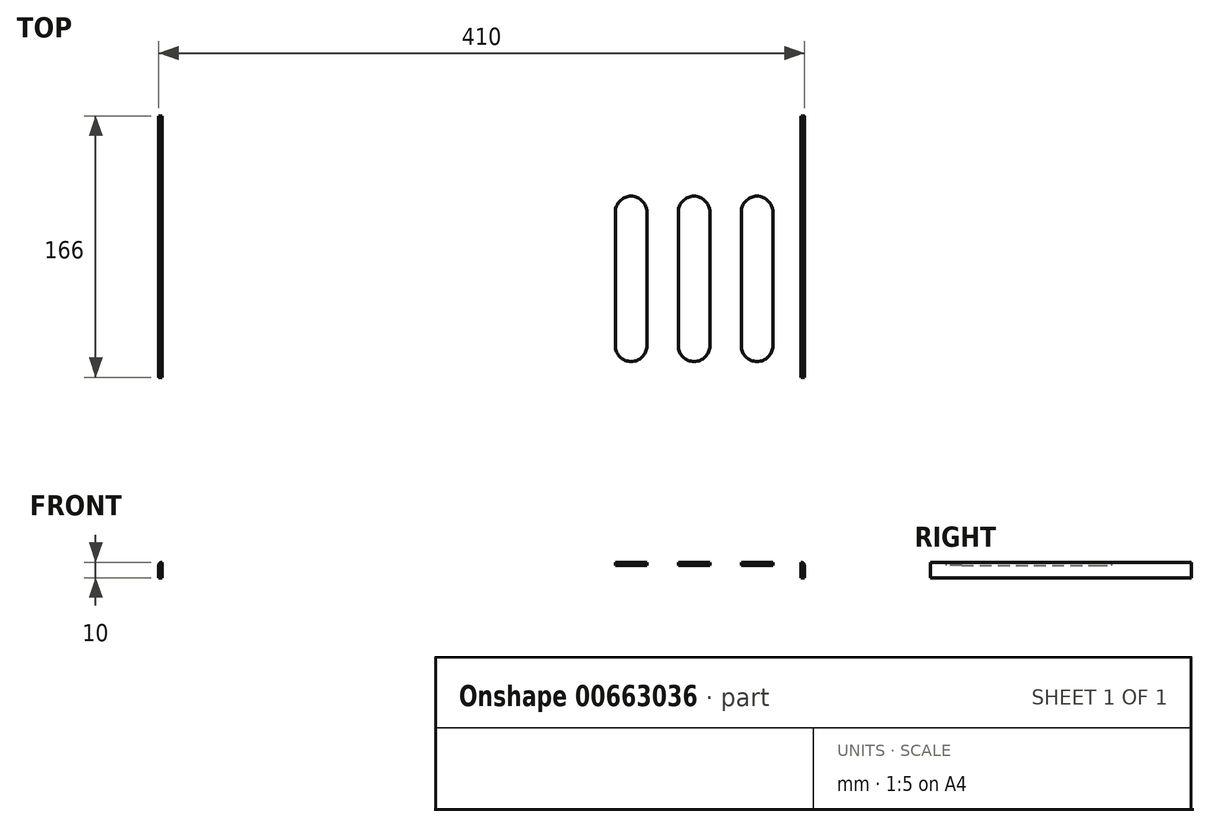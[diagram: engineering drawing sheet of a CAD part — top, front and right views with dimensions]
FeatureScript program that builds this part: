
annotation { "Feature Type Name" : "Feature", "Feature Type Description" : "" }
export const myFeature = defineFeature(function(context is Context, id is Id, definition is map)
    precondition{}
    {
        {
            var Q0;
            Q0=qCreatedBy(makeId("Front.planeOp"),FACE);
            var sketch = newSketch(context, id + "F0", { "sketchPlane" : qUnion([Q0])});
            skLineSegment(sketch, "E0", {"start": v(0, 0) * mm, "end": v(0, 8) * mm});
            skLineSegment(sketch, "E1", {"start": v(2, 10) * mm, "end": v(408, 10) * mm});
            skLineSegment(sketch, "E2", {"start": v(410, 8) * mm, "end": v(410, 0) * mm});
            skLineSegment(sketch, "E3.0", {"start": v(408, 8) * mm, "end": v(408, 0) * mm});
            skLineSegment(sketch, "E3.1", {"start": v(2, 8) * mm, "end": v(408, 8) * mm});
            skLineSegment(sketch, "E3.2", {"start": v(2, 0) * mm, "end": v(2, 8) * mm});
            skLineSegment(sketch, "E4", {"start": v(408, 0) * mm, "end": v(410, 0) * mm});
            skLineSegment(sketch, "E5", {"start": v(0, 0) * mm, "end": v(2, 0) * mm});
            skPoint(sketch, "E6.visualSharp", {"position": v(410, 10) * mm});
            skArc(sketch, "E6.filletArc", {"start": v(410, 8) * mm, "mid": v(409.41, 9.41) * mm, "end": v(408, 10) * mm});
            skPoint(sketch, "E7.visualSharp", {"position": v(0, 10) * mm});
            skArc(sketch, "E7.filletArc", {"start": v(2, 10) * mm, "mid": v(0.59, 9.41) * mm, "end": v(0, 8) * mm});
            skSolve(sketch);
        }
        {
            var Q0;
            Q0=makeQuery(id+"F0.imprint","IMPRINT",FACE,{"disambiguationData":[TD([[makeQuery(id+"F0.imprint","IMPRINT",EDGE,{"derivedFrom":sQuery(id+"F0.wireOp",EDGE,"E0")}),-1.0]])]});
            extrude(context, id + "F1", {"entities" : qUnion([Q0]), "oppositeDirection" : true, "depth" : 166 * mm, "offsetDistance" : 25 * mm});
        }
        {
            var Q0;
            Q0=makeQuery(id+"F1.opExtrude","SWEPT_FACE",FACE,{"disambiguationData":[OSD([sQuery(id+"F0.wireOp",EDGE,"E3.1")])]});
            var sketch = newSketch(context, id + "F2", { "sketchPlane" : qUnion([Q0])});
            skPoint(sketch, "E8", {"position": v(300, -62.5) * mm});
            skPoint(sketch, "E9", {"position": v(340, -62.5) * mm});
            skPoint(sketch, "E10", {"position": v(380, -62.5) * mm});
            skPoint(sketch, "E11", {"position": v(300, -166) * mm});
            skPoint(sketch, "E12", {"position": v(340, -166) * mm});
            skPoint(sketch, "E13", {"position": v(380, -166) * mm});
            skLineSegment(sketch, "E14", {"start": v(300, -20) * mm, "end": v(300, -105) * mm});
            skArc(sketch, "E15.0.startCap", {"start": v(290, -20) * mm, "mid": v(300, -10) * mm, "end": v(310, -20) * mm});
            skArc(sketch, "E15.0.endCap", {"start": v(310, -105) * mm, "mid": v(300, -115) * mm, "end": v(290, -105) * mm});
            skLineSegment(sketch, "E15.0.left", {"start": v(310, -20) * mm, "end": v(310, -105) * mm});
            skLineSegment(sketch, "E15.0.right", {"start": v(290, -20) * mm, "end": v(290, -105) * mm});
            skLineSegment(sketch, "E16", {"start": v(340, -20) * mm, "end": v(340, -105) * mm});
            skLineSegment(sketch, "E17", {"start": v(380, -20) * mm, "end": v(380, -105) * mm});
            skArc(sketch, "E18.0.startCap", {"start": v(330, -20) * mm, "mid": v(340, -10) * mm, "end": v(350, -20) * mm});
            skArc(sketch, "E18.0.endCap", {"start": v(350, -105) * mm, "mid": v(340, -115) * mm, "end": v(330, -105) * mm});
            skLineSegment(sketch, "E18.0.left", {"start": v(350, -20) * mm, "end": v(350, -105) * mm});
            skLineSegment(sketch, "E18.0.right", {"start": v(330, -20) * mm, "end": v(330, -105) * mm});
            skArc(sketch, "E18.1.startCap", {"start": v(370, -20) * mm, "mid": v(380, -10) * mm, "end": v(390, -20) * mm});
            skArc(sketch, "E18.1.endCap", {"start": v(390, -105) * mm, "mid": v(380, -115) * mm, "end": v(370, -105) * mm});
            skLineSegment(sketch, "E18.1.left", {"start": v(390, -20) * mm, "end": v(390, -105) * mm});
            skLineSegment(sketch, "E18.1.right", {"start": v(370, -20) * mm, "end": v(370, -105) * mm});
            skSolve(sketch);
        }
        {
            var Q0;
            Q0=makeQuery(id+"F2.imprint","IMPRINT",FACE,{"disambiguationData":[TD([[makeQuery(id+"F2.imprint","IMPRINT",EDGE,{"derivedFrom":sQuery(id+"F2.wireOp",EDGE,"E15.0.startCap")}),-1.0]])]});
            var Q1;
            Q1=makeQuery(id+"F2.imprint","IMPRINT",FACE,{"disambiguationData":[TD([[makeQuery(id+"F2.imprint","IMPRINT",EDGE,{"derivedFrom":sQuery(id+"F2.wireOp",EDGE,"E18.0.startCap")}),-1.0]])]});
            var Q2;
            Q2=makeQuery(id+"F2.imprint","IMPRINT",FACE,{"disambiguationData":[TD([[makeQuery(id+"F2.imprint","IMPRINT",EDGE,{"derivedFrom":sQuery(id+"F2.wireOp",EDGE,"E18.1.startCap")}),-1.0]])]});
            extrude(context, id + "F3", {"entities" : qUnion([Q0, Q1, Q2]), "operationType" : NewBodyOperationType.REMOVE, "endBound" : BoundingType.UP_TO_NEXT, "oppositeDirection" : true, "depth" : 25 * mm, "offsetDistance" : 25 * mm});
        }
        {
            var Q0;
            Q0=sQuery(id+"F2.wireOp",VERTEX,"E11");
            var Q1;
            Q1=sQuery(id+"F2.wireOp",VERTEX,"E12");
            var Q2;
            Q2=sQuery(id+"F2.wireOp",VERTEX,"E13");
            var Q3;
            Q3=makeQuery(id+"F1.opExtrude","SWEPT_BODY",BODY,{"disambiguationData":[OSD([sQuery(id+"F0.wireOp",EDGE,"E0"),sQuery(id+"F0.wireOp",EDGE,"E1"),sQuery(id+"F0.wireOp",EDGE,"E2"),sQuery(id+"F0.wireOp",EDGE,"E3.0"),sQuery(id+"F0.wireOp",EDGE,"E3.1"),sQuery(id+"F0.wireOp",EDGE,"E3.2"),sQuery(id+"F0.wireOp",EDGE,"E4"),sQuery(id+"F0.wireOp",EDGE,"E5"),sQuery(id+"F0.wireOp",EDGE,"E6.filletArc"),sQuery(id+"F0.wireOp",EDGE,"E7.filletArc")])]});
            hole(context, id + "F4", {"style" : HoleStyle.SIMPLE, "endStyle" : HoleEndStyle.BLIND, "holeDiameter" : 20 * mm, "majorDiameter" : 5 * mm, "holeDepth" : 5 * mm, "isTappedThrough" : true, "tappedDepth" : 12 * mm, "tapClearance" : 3, "locations" : qUnion([Q0, Q1, Q2]), "scope" : qUnion([Q3])});
        }
    });
